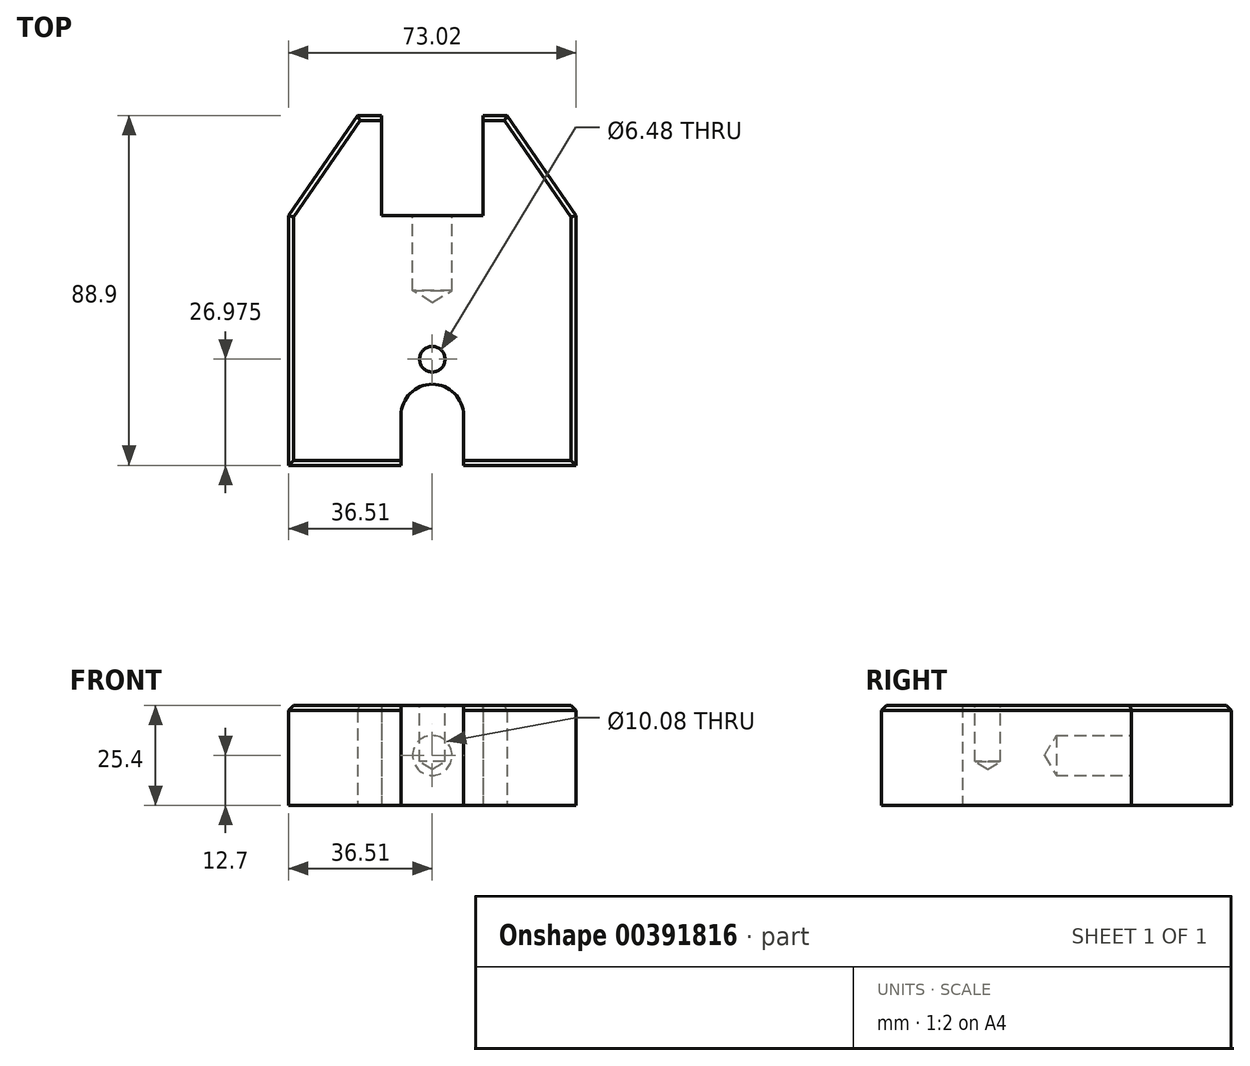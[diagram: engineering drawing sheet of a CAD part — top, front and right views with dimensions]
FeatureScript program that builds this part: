
annotation { "Feature Type Name" : "Feature", "Feature Type Description" : "" }
export const myFeature = defineFeature(function(context is Context, id is Id, definition is map)
    precondition{}
    {
        {
            var Q0;
            Q0=qCreatedBy(makeId("Top.planeOp"),FACE);
            var sketch = newSketch(context, id + "F0", { "sketchPlane" : qUnion([Q0])});
            skLineSegment(sketch, "E0.bottom", {"start": v(-18.99, 0) * mm, "end": v(-12.9, 0) * mm});
            skLineSegment(sketch, "E0.top", {"start": v(-36.51, -88.9) * mm, "end": v(-7.94, -88.9) * mm});
            skLineSegment(sketch, "E0.left", {"start": v(-36.51, -25.4) * mm, "end": v(-36.51, -88.9) * mm});
            skLineSegment(sketch, "E0.right", {"start": v(36.51, -25.4) * mm, "end": v(36.51, -88.9) * mm});
            skArc(sketch, "E1", {"start": v(7.94, -76.21) * mm, "mid": v(0, -68.28) * mm, "end": v(-7.94, -76.21) * mm});
            skLineSegment(sketch, "E2", {"start": v(-7.94, -76.21) * mm, "end": v(-7.94, -88.9) * mm});
            skLineSegment(sketch, "E3", {"start": v(7.94, -76.21) * mm, "end": v(7.94, -88.9) * mm});
            skLineSegment(sketch, "E4.top", {"start": v(-12.9, -25.4) * mm, "end": v(12.9, -25.4) * mm});
            skLineSegment(sketch, "E4.left", {"start": v(-12.9, 0) * mm, "end": v(-12.9, -25.4) * mm});
            skLineSegment(sketch, "E4.right", {"start": v(12.9, 0) * mm, "end": v(12.9, -25.4) * mm});
            skLineSegment(sketch, "E5", {"start": v(-36.51, -25.4) * mm, "end": v(-18.99, 0) * mm});
            skLineSegment(sketch, "E6", {"start": v(18.99, 0) * mm, "end": v(36.51, -25.4) * mm});
            skPoint(sketch, "E7.orphan", {"position": v(-36.51, 0) * mm});
            skLineSegment(sketch, "E8.trimOffspring", {"start": v(12.9, 0) * mm, "end": v(18.99, 0) * mm});
            skPoint(sketch, "E9.orphan", {"position": v(36.51, 0) * mm});
            skLineSegment(sketch, "E10.trimOffspring", {"start": v(7.94, -88.9) * mm, "end": v(36.51, -88.9) * mm});
            skSolve(sketch);
        }
        {
            var Q0;
            Q0=makeQuery(id+"F0.imprint","IMPRINT",FACE,{"disambiguationData":[TD([[makeQuery(id+"F0.imprint","IMPRINT",EDGE,{"derivedFrom":sQuery(id+"F0.wireOp",EDGE,"E0.bottom")}),-1.0]])]});
            extrude(context, id + "F1", {"entities" : qUnion([Q0]), "depth" : 25.4 * mm});
        }
        {
            var Q0;
            Q0=makeQuery(id+"F1.opExtrude","SWEPT_FACE",FACE,{"disambiguationData":[OSD([sQuery(id+"F0.wireOp",EDGE,"E4.top")])]});
            var sketch = newSketch(context, id + "F2", { "sketchPlane" : qUnion([Q0])});
            skPoint(sketch, "E11", {"position": v(0, 12.7) * mm});
            skSolve(sketch);
        }
        {
            var Q0;
            Q0=sQuery(id+"F2.wireOp",VERTEX,"E11");
            var Q1;
            Q1=makeQuery(id+"F1.opExtrude","SWEPT_BODY",BODY,{"disambiguationData":[OSD([sQuery(id+"F0.wireOp",EDGE,"E0.bottom"),sQuery(id+"F0.wireOp",EDGE,"E0.top"),sQuery(id+"F0.wireOp",EDGE,"E0.left"),sQuery(id+"F0.wireOp",EDGE,"E0.right"),sQuery(id+"F0.wireOp",EDGE,"E1"),sQuery(id+"F0.wireOp",EDGE,"E2"),sQuery(id+"F0.wireOp",EDGE,"E3"),sQuery(id+"F0.wireOp",EDGE,"E4.top"),sQuery(id+"F0.wireOp",EDGE,"E4.left"),sQuery(id+"F0.wireOp",EDGE,"E4.right"),sQuery(id+"F0.wireOp",EDGE,"E5"),sQuery(id+"F0.wireOp",EDGE,"E6"),sQuery(id+"F0.wireOp",EDGE,"E8.trimOffspring"),sQuery(id+"F0.wireOp",EDGE,"E10.trimOffspring")])]});
            hole(context, id + "F3", {"style" : HoleStyle.SIMPLE, "endStyle" : HoleEndStyle.BLIND, "standardTappedOrClearance" : lookupTablePath({ "standard" : "ANSI", "fit" : "Normal (ASME)", "size" : "3/8", "type" : "Clearance" }), "standardBlindInLast" : lookupTablePath({ "fit" : "Free", "standard" : "ANSI", "size" : "3/8", "type" : "Clearance" }), "holeDiameter" : 10.08 * mm, "holeDepth" : 19.05 * mm, "isTappedThrough" : true, "tappedDepth" : 12.7 * mm, "tapClearance" : 3, "locations" : qUnion([Q0]), "scope" : qUnion([Q1])});
        }
        {
            var Q0;
            Q0=makeQuery(id+"F1.opExtrude","CAP_FACE",FACE,{"disambiguationData":[OSD([sQuery(id+"F0.wireOp",EDGE,"E0.bottom"),sQuery(id+"F0.wireOp",EDGE,"E0.top"),sQuery(id+"F0.wireOp",EDGE,"E0.left"),sQuery(id+"F0.wireOp",EDGE,"E0.right"),sQuery(id+"F0.wireOp",EDGE,"E1"),sQuery(id+"F0.wireOp",EDGE,"E2"),sQuery(id+"F0.wireOp",EDGE,"E3"),sQuery(id+"F0.wireOp",EDGE,"E4.top"),sQuery(id+"F0.wireOp",EDGE,"E4.left"),sQuery(id+"F0.wireOp",EDGE,"E4.right"),sQuery(id+"F0.wireOp",EDGE,"E5"),sQuery(id+"F0.wireOp",EDGE,"E6"),sQuery(id+"F0.wireOp",EDGE,"E8.trimOffspring"),sQuery(id+"F0.wireOp",EDGE,"E10.trimOffspring")])],"isStart":false});
            var sketch = newSketch(context, id + "F4", { "sketchPlane" : qUnion([Q0])});
            skPoint(sketch, "E12", {"position": v(0, -61.93) * mm});
            skSolve(sketch);
        }
        {
            var Q0;
            Q0=sQuery(id+"F4.wireOp",VERTEX,"E12");
            var Q1;
            Q1=makeQuery(id+"F1.opExtrude","SWEPT_BODY",BODY,{"disambiguationData":[OSD([sQuery(id+"F0.wireOp",EDGE,"E0.bottom"),sQuery(id+"F0.wireOp",EDGE,"E0.top"),sQuery(id+"F0.wireOp",EDGE,"E0.left"),sQuery(id+"F0.wireOp",EDGE,"E0.right"),sQuery(id+"F0.wireOp",EDGE,"E1"),sQuery(id+"F0.wireOp",EDGE,"E2"),sQuery(id+"F0.wireOp",EDGE,"E3"),sQuery(id+"F0.wireOp",EDGE,"E4.top"),sQuery(id+"F0.wireOp",EDGE,"E4.left"),sQuery(id+"F0.wireOp",EDGE,"E4.right"),sQuery(id+"F0.wireOp",EDGE,"E5"),sQuery(id+"F0.wireOp",EDGE,"E6"),sQuery(id+"F0.wireOp",EDGE,"E8.trimOffspring"),sQuery(id+"F0.wireOp",EDGE,"E10.trimOffspring")])]});
            hole(context, id + "F5", {"style" : HoleStyle.SIMPLE, "endStyle" : HoleEndStyle.BLIND, "holeDiameter" : 6.48 * mm, "holeDepth" : 14.27 * mm, "isTappedThrough" : true, "tappedDepth" : 12.7 * mm, "tapClearance" : 3, "locations" : qUnion([Q0]), "scope" : qUnion([Q1])});
        }
        {
            var Q0;
            Q0=makeQuery(id+"F1.opExtrude","CAP_EDGE",EDGE,{"disambiguationData":[OSD([sQuery(id+"F0.wireOp",EDGE,"E0.top")])],"isStart":false});
            var Q1;
            Q1=makeQuery(id+"F1.opExtrude","CAP_EDGE",EDGE,{"disambiguationData":[OSD([sQuery(id+"F0.wireOp",EDGE,"E0.bottom")])],"isStart":false});
            var Q2;
            Q2=makeQuery(id+"F1.opExtrude","CAP_EDGE",EDGE,{"disambiguationData":[OSD([sQuery(id+"F0.wireOp",EDGE,"E5")])],"isStart":false});
            var Q3;
            Q3=makeQuery(id+"F1.opExtrude","CAP_EDGE",EDGE,{"disambiguationData":[OSD([sQuery(id+"F0.wireOp",EDGE,"E0.left")])],"isStart":false});
            var Q4;
            Q4=makeQuery(id+"F1.opExtrude","CAP_EDGE",EDGE,{"disambiguationData":[OSD([sQuery(id+"F0.wireOp",EDGE,"E8.trimOffspring")])],"isStart":false});
            var Q5;
            Q5=makeQuery(id+"F1.opExtrude","CAP_EDGE",EDGE,{"disambiguationData":[OSD([sQuery(id+"F0.wireOp",EDGE,"E6")])],"isStart":false});
            var Q6;
            Q6=makeQuery(id+"F1.opExtrude","CAP_EDGE",EDGE,{"disambiguationData":[OSD([sQuery(id+"F0.wireOp",EDGE,"E0.right")])],"isStart":false});
            var Q7;
            Q7=makeQuery(id+"F1.opExtrude","CAP_EDGE",EDGE,{"disambiguationData":[OSD([sQuery(id+"F0.wireOp",EDGE,"E10.trimOffspring")])],"isStart":false});
            chamfer(context, id + "F6", {"entities" : qUnion([Q0, Q1, Q2, Q3, Q4, Q5, Q6, Q7]), "width" : 1.27 * mm, "tangentPropagation" : true});
        }
    });
